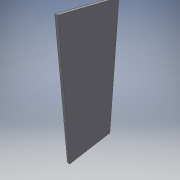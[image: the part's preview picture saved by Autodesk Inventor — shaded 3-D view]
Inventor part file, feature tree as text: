
AUTODESK INVENTOR PART (.ipt)
format: ipt  version: 2016 (Build 200138000, 138)  size: 87,552 bytes
history: native  units: in
note: dims shown in document units (in); Inventor stores cm internally (conversion verified against a paired STEP export)
features: extrude x1, sketch x1
ambient origin geometry x8: Origin, YZ Plane, XZ Plane, XY Plane, X Axis, Y Axis, Z Axis, Center Point
bodies: Solid1 (feature_tree)
feature tree (2):
  extrude  "Extrusion1"  Depth=44.0in
  sketch  "Sketch1"  dims[d0=18.0in d1=44.0in d2=1.0in d3=0.0in]
